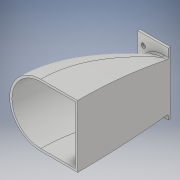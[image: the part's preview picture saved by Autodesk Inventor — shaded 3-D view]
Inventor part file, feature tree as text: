
AUTODESK INVENTOR PART (.ipt)
format: ipt  version: 2019 (Build 230136000, 136)  size: 304,128 bytes
history: native  units: mm
features: sketch x5, extrude x2, loft x2, plane x1, fillet x1, other x1
ambient origin geometry x8: Origin, YZ Plane, XZ Plane, XY Plane, X Axis, Y Axis, Z Axis, Center Point
bodies: Solid1 (feature_tree)
feature tree (12):
  extrude  "Extrusion1"  Depth=26.0mm
  sketch  "Sketch2"  dims[d2=40.0mm d3=55.0mm]
  plane  "Work Plane1"
  loft  "Loft1"
  loft  "Loft2"
  extrude  "Extrusion2"  Depth=2.0mm
  fillet  "Fillet1"  Radius=80.0mm
  sketch  "Sketch1"  dims[d0=24.0mm d1=26.0mm]
  sketch  "Sketch3"  dims[d4=27.0mm d5=2.0mm d6=0.0mm]
  sketch  "Sketch4"  dims[d7=42.0mm d9=2.0mm d10=80.0mm]
  other  "Edges1"
  sketch  "Sketch5"  dims[d11=60.0mm d12=10.0mm d13=90.0deg d14=0.0mm d15=90.0deg d16=2.0mm d17=2.0mm d18=10.0mm d19=90.0deg d20=0.0mm d21=90.0deg d22=25.5mm d23=4.0mm d24=4.0mm d25=5.0mm d26=9.0mm d27=5.0mm d28=2.0mm d29=0.0mm d30=1.1mm]
